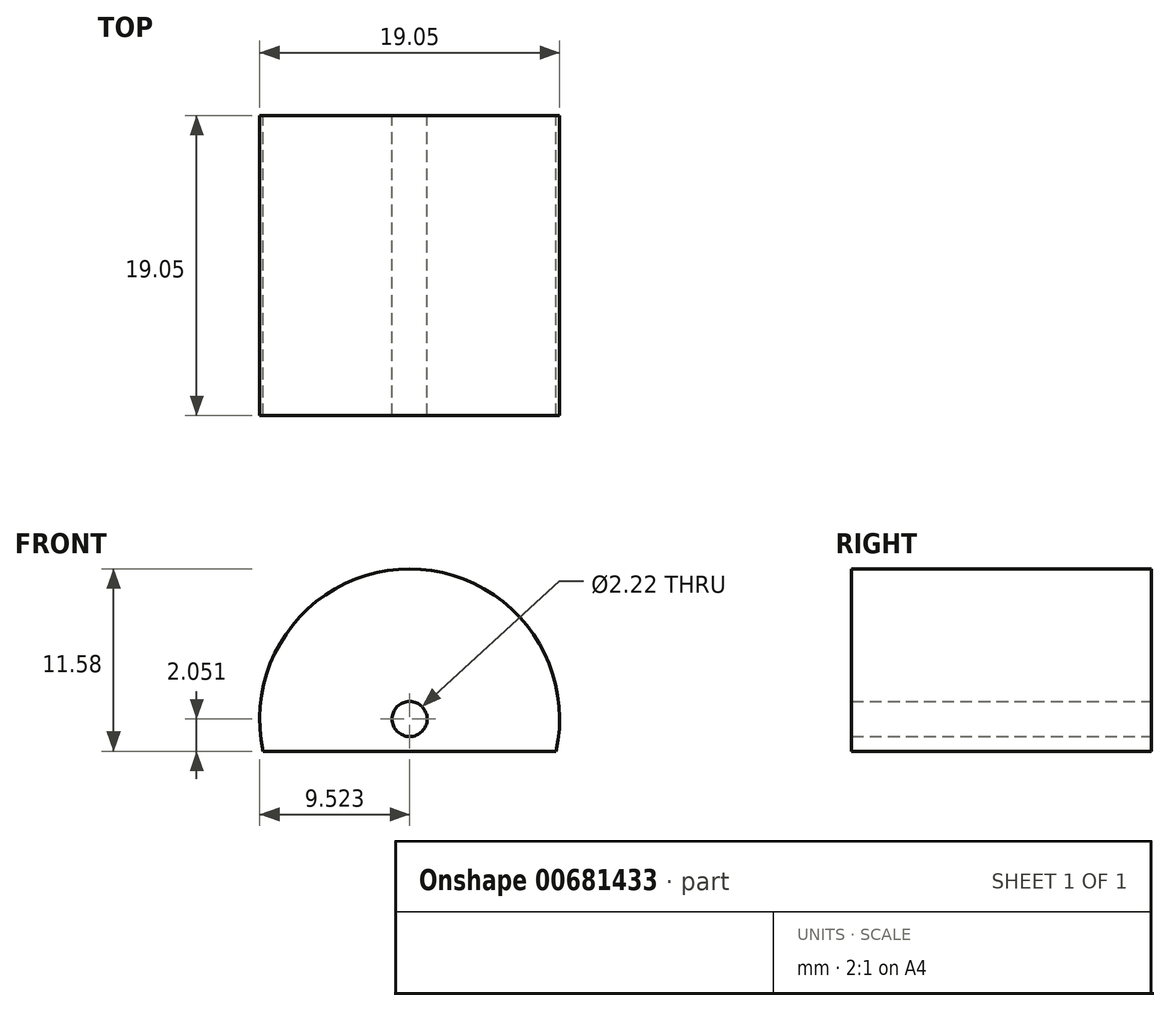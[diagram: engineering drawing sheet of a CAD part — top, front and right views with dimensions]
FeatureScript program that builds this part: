
annotation { "Feature Type Name" : "Feature", "Feature Type Description" : "" }
export const myFeature = defineFeature(function(context is Context, id is Id, definition is map)
    precondition{}
    {
        {
            var Q0;
            Q0=qCreatedBy(makeId("Front.planeOp"),FACE);
            var sketch = newSketch(context, id + "F0", { "sketchPlane" : qUnion([Q0])});
            skCircle(sketch, "E0", {"center": v(-29.3, 40.74) * mm, "radius": 9.53 * mm});
            skLineSegment(sketch, "E1", {"start": v(-38.6, 38.7) * mm, "end": v(-20, 38.7) * mm});
            skCircle(sketch, "E2", {"center": v(-29.3, 40.74) * mm, "radius": 1.11 * mm});
            skSolve(sketch);
        }
        {
            var Q0;
            {var subQ0=sQuery(id+"F0.wireOp",EDGE,"E1");Q0=makeQuery(id+"F0.imprint","IMPRINT",FACE,{"disambiguationData":[TD([[makeQuery(id+"F0.imprint","IMPRINT",EDGE,{"derivedFrom":subQ0}),1.0]])]});}
            extrude(context, id + "F1", {"entities" : qUnion([Q0]), "depth" : 19.05 * mm, "offsetDistance" : 25.4 * mm});
        }
    });
